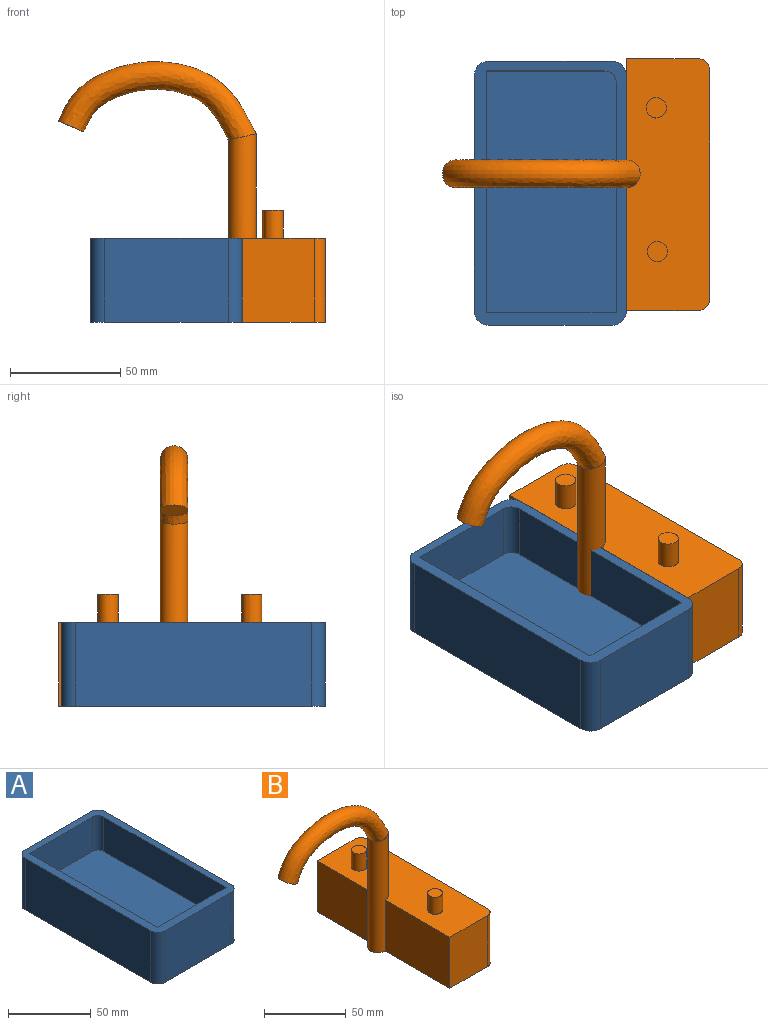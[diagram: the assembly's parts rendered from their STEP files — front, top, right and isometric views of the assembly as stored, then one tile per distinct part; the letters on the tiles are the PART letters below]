
ASSEMBLY  parts=2 mates=1
PART A: 16 faces, bbox 68.9x119.8x38.1 mm
  f0: cylinder r=6.35mm len=38.1mm, axis (0,0,-1), area 380mm2, adj f1,f11,f12,f13
  f1: plane 56.25x38.1mm, normal (0,1,0), area 2143.1mm2, adj f0,f2,f12,f13
  f2: cylinder r=6.35mm len=38.1mm, axis (0,0,-1), area 380mm2, adj f1,f3,f12,f13
  f3: plane 107.13x38.1mm, normal (-1,0,0), area 4081.7mm2, adj f2,f4,f12,f13
  f4: cylinder r=6.35mm len=38.1mm, axis (0,0,-1), area 380mm2, adj f3,f5,f12,f13
  f5: plane 56.25x38.1mm, normal (0,-1,0), area 2143.1mm2, adj f4,f6,f12,f13
  f6: cylinder r=6.35mm len=38.1mm, axis (0,0,-1), area 380mm2, adj f5,f11,f12,f13
  f7: plane 58.99x25.4mm, normal (0,1,0), area 1498.4mm2, adj f8,f10,f12,f14
  f8: plane 109.51x25.4mm, normal (1,0,0), area 2781.5mm2, adj f7,f9,f12,f14
  f9: plane 53.91x25.4mm, normal (0,-1,0), area 1369.4mm2, adj f8,f12,f14,f15
  f10: plane 104.43x25.4mm, normal (-1,0,0), area 2652.4mm2, adj f7,f12,f14,f15
  f11: plane 107.13x38.1mm, normal (1,0,0), area 4081.7mm2, adj f0,f6,f12,f13
  f12: plane 119.83x68.95mm, normal (0,0,1), area 1772.9mm2, adj f0,f1,f2,f3,f4,f5,f6,f7
  f13: plane 119.83x68.95mm, normal (0,0,-1), area 8227.6mm2, adj f0,f1,f2,f3,f4,f5,f6,f11
  f14: plane 109.51x58.99mm, normal (0,0,1), area 6454.7mm2, adj f7,f8,f9,f10,f15
  f15: cylinder r=5.08mm len=25.4mm, axis (0,0,1), area 202.7mm2, adj f9,f10,f12,f14
PART B: 16 faces, bbox 121.2x114.3x118.5 mm
  f0: cylinder r=6.27mm len=85.62mm, axis (0,0,1), area 2561.3mm2, adj f2,f3,f4,f5,f9
  f1: plane 12.54x11.51mm, normal (-0.4,0,-0.92), area 123.5mm2, adj f3
  f2: plane 114.3x44.03mm, normal (0,0,-1), area 4366.3mm2, adj f0,f4,f5,f6,f7,f8,f10,f11
  f3: bspline ~89.84x38.71mm, area 3923.9mm2, adj f0,f1
  f4: plane 46.07x38.1mm, normal (-1,0,0), area 1755.4mm2, adj f0,f2,f8,f9
  f5: plane 55.68x38.1mm, normal (-1,0,0), area 2121.6mm2, adj f0,f2,f6,f9
  f6: plane 38.1x32.68mm, normal (0,-1,0), area 1245mm2, adj f2,f5,f9,f10
  f7: plane 104.14x38.1mm, normal (1,0,0), area 3967.7mm2, adj f2,f9,f10,f11
  f8: plane 38.1x32.68mm, normal (0,1,0), area 1245mm2, adj f2,f4,f9,f11
  f9: plane 114.3x37.76mm, normal (0,0,1), area 4110.4mm2, adj f0,f4,f5,f6,f7,f8,f10,f11
  f10: cylinder r=5.08mm len=38.1mm, axis (0,0,1), area 304mm2, adj f2,f6,f7,f9
  f11: cylinder r=5.08mm len=38.1mm, axis (0,0,-1), area 304mm2, adj f2,f7,f8,f9
  f12: cylinder r=4.55mm len=12.7mm, axis (0,0,-1), area 363.3mm2, adj f9,f13
  f13: plane 9.1x9.1mm, normal (0,0,1), area 65.1mm2, adj f12
  f14: cylinder r=4.63mm len=12.7mm, axis (0,0,-1), area 369.3mm2, adj f9,f15
  f15: plane 9.26x9.26mm, normal (0,0,1), area 67.3mm2, adj f14
PLACE A t=(30.75,0.78,-11.4)mm
PLACE B t=(30.75,5.07,-11.4)mm
MATE fastened A.f11 <-> B.f5  axis (1,0,0) through (30.75,-3.64,7.65)mm
